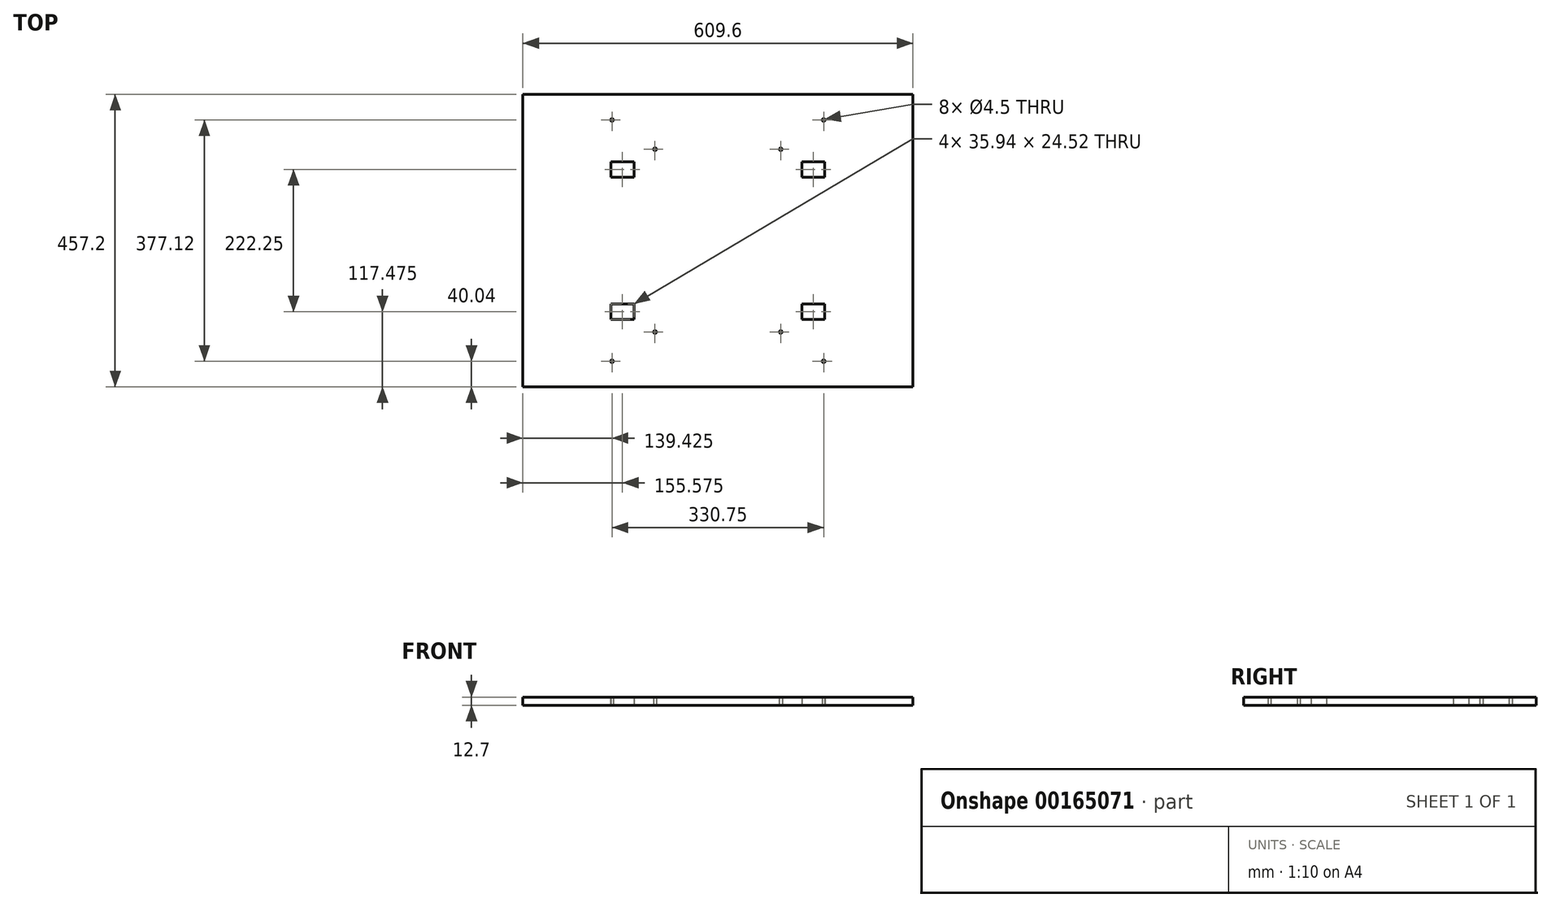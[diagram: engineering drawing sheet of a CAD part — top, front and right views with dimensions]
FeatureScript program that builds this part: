
annotation { "Feature Type Name" : "Feature", "Feature Type Description" : "" }
export const myFeature = defineFeature(function(context is Context, id is Id, definition is map)
    precondition{}
    {
        {
            var Q0;
            Q0=qCreatedBy(makeId("Top.planeOp"),FACE);
            var sketch = newSketch(context, id + "F0", { "sketchPlane" : qUnion([Q0])});
            skLineSegment(sketch, "E0.bottom", {"start": v(-304.8, 228.6) * mm, "end": v(304.8, 228.6) * mm});
            skLineSegment(sketch, "E0.top", {"start": v(-304.8, -228.6) * mm, "end": v(304.8, -228.6) * mm});
            skLineSegment(sketch, "E0.left", {"start": v(-304.8, 228.6) * mm, "end": v(-304.8, -228.6) * mm});
            skLineSegment(sketch, "E0.right", {"start": v(304.8, 228.6) * mm, "end": v(304.8, -228.6) * mm});
            skPoint(sketch, "E0.middle", {"position": v(0, 0) * mm});
            skLineSegment(sketch, "E1.bottom", {"start": v(-149.22, 111.13) * mm, "end": v(149.23, 111.13) * mm, "construction": true});
            skLineSegment(sketch, "E1.top", {"start": v(-149.22, -111.13) * mm, "end": v(149.23, -111.13) * mm, "construction": true});
            skLineSegment(sketch, "E1.left", {"start": v(-149.22, 111.13) * mm, "end": v(-149.22, -111.13) * mm, "construction": true});
            skLineSegment(sketch, "E1.right", {"start": v(149.22, 111.13) * mm, "end": v(149.23, -111.13) * mm, "construction": true});
            skLineSegment(sketch, "E2", {"start": v(98.27, 142.86) * mm, "end": v(149.22, 142.86) * mm, "construction": true});
            skLineSegment(sketch, "E3", {"start": v(149.22, 142.86) * mm, "end": v(165.38, 142.86) * mm, "construction": true});
            skLineSegment(sketch, "E4", {"start": v(165.38, 142.86) * mm, "end": v(165.38, 188.56) * mm, "construction": true});
            skLineSegment(sketch, "E5", {"start": v(149.22, 142.86) * mm, "end": v(149.22, 123.38) * mm, "construction": true});
            skCircle(sketch, "E6", {"center": v(98.27, 142.86) * mm, "radius": 2.25 * mm});
            skCircle(sketch, "E7", {"center": v(165.38, 188.56) * mm, "radius": 2.25 * mm});
            skLineSegment(sketch, "E8.bottom", {"start": v(131.25, 123.38) * mm, "end": v(167.2, 123.38) * mm});
            skLineSegment(sketch, "E8.top", {"start": v(131.25, 98.87) * mm, "end": v(167.2, 98.87) * mm});
            skLineSegment(sketch, "E8.left", {"start": v(131.25, 123.38) * mm, "end": v(131.25, 98.87) * mm});
            skLineSegment(sketch, "E8.right", {"start": v(167.2, 123.38) * mm, "end": v(167.2, 98.87) * mm});
            skPoint(sketch, "E8.middle", {"position": v(149.23, 111.13) * mm});
            skLineSegment(sketch, "E9.bottom", {"start": v(-131.25, 98.87) * mm, "end": v(-167.2, 98.87) * mm});
            skLineSegment(sketch, "E9.top", {"start": v(-131.25, 123.38) * mm, "end": v(-167.2, 123.38) * mm});
            skLineSegment(sketch, "E9.left", {"start": v(-131.25, 98.87) * mm, "end": v(-131.25, 123.38) * mm});
            skLineSegment(sketch, "E9.right", {"start": v(-167.2, 98.87) * mm, "end": v(-167.2, 123.38) * mm});
            skPoint(sketch, "E9.middle", {"position": v(-149.23, 111.13) * mm});
            skLineSegment(sketch, "E10.bottom", {"start": v(-131.25, -123.38) * mm, "end": v(-167.2, -123.38) * mm});
            skLineSegment(sketch, "E10.top", {"start": v(-131.25, -98.87) * mm, "end": v(-167.2, -98.87) * mm});
            skLineSegment(sketch, "E10.left", {"start": v(-131.25, -123.38) * mm, "end": v(-131.25, -98.87) * mm});
            skLineSegment(sketch, "E10.right", {"start": v(-167.2, -123.38) * mm, "end": v(-167.2, -98.87) * mm});
            skPoint(sketch, "E10.middle", {"position": v(-149.23, -111.13) * mm});
            skLineSegment(sketch, "E11.bottom", {"start": v(131.25, -123.38) * mm, "end": v(167.2, -123.38) * mm});
            skLineSegment(sketch, "E11.top", {"start": v(131.25, -98.87) * mm, "end": v(167.2, -98.87) * mm});
            skLineSegment(sketch, "E11.left", {"start": v(131.25, -123.38) * mm, "end": v(131.25, -98.87) * mm});
            skLineSegment(sketch, "E11.right", {"start": v(167.2, -123.38) * mm, "end": v(167.2, -98.87) * mm});
            skPoint(sketch, "E11.middle", {"position": v(149.23, -111.13) * mm});
            skLineSegment(sketch, "E12", {"start": v(-149.22, 123.38) * mm, "end": v(-149.22, 142.86) * mm, "construction": true});
            skLineSegment(sketch, "E13", {"start": v(-149.23, 142.86) * mm, "end": v(-98.27, 142.86) * mm, "construction": true});
            skLineSegment(sketch, "E14", {"start": v(-149.23, 142.86) * mm, "end": v(-165.38, 142.86) * mm, "construction": true});
            skLineSegment(sketch, "E15", {"start": v(-165.38, 142.86) * mm, "end": v(-165.38, 188.56) * mm, "construction": true});
            skLineSegment(sketch, "E16", {"start": v(-149.22, -123.38) * mm, "end": v(-149.22, -142.86) * mm, "construction": true});
            skLineSegment(sketch, "E17", {"start": v(-149.23, -142.86) * mm, "end": v(-165.38, -142.86) * mm, "construction": true});
            skLineSegment(sketch, "E18", {"start": v(-165.38, -142.86) * mm, "end": v(-165.38, -188.56) * mm, "construction": true});
            skLineSegment(sketch, "E19", {"start": v(-149.23, -142.86) * mm, "end": v(-98.27, -142.86) * mm, "construction": true});
            skLineSegment(sketch, "E20", {"start": v(149.22, -123.38) * mm, "end": v(149.22, -142.86) * mm, "construction": true});
            skLineSegment(sketch, "E21", {"start": v(149.22, -142.86) * mm, "end": v(165.38, -142.86) * mm, "construction": true});
            skLineSegment(sketch, "E22", {"start": v(165.38, -142.86) * mm, "end": v(165.38, -188.56) * mm, "construction": true});
            skLineSegment(sketch, "E23", {"start": v(149.22, -142.86) * mm, "end": v(98.27, -142.86) * mm, "construction": true});
            skLineSegment(sketch, "E24.bottom", {"start": v(6.35, 6.35) * mm, "end": v(-6.35, 6.35) * mm, "construction": true});
            skLineSegment(sketch, "E24.top", {"start": v(6.35, -6.35) * mm, "end": v(-6.35, -6.35) * mm, "construction": true});
            skLineSegment(sketch, "E24.left", {"start": v(6.35, 6.35) * mm, "end": v(6.35, -6.35) * mm, "construction": true});
            skLineSegment(sketch, "E24.right", {"start": v(-6.35, 6.35) * mm, "end": v(-6.35, -6.35) * mm, "construction": true});
            skLineSegment(sketch, "E25.bottom", {"start": v(6.35, 6.35) * mm, "end": v(292.1, 6.35) * mm, "construction": true});
            skLineSegment(sketch, "E25.top", {"start": v(6.35, 215.9) * mm, "end": v(292.1, 215.9) * mm, "construction": true});
            skLineSegment(sketch, "E25.left", {"start": v(6.35, 6.35) * mm, "end": v(6.35, 215.9) * mm, "construction": true});
            skLineSegment(sketch, "E25.right", {"start": v(292.1, 6.35) * mm, "end": v(292.1, 215.9) * mm, "construction": true});
            skLineSegment(sketch, "E26", {"start": v(292.1, 215.9) * mm, "end": v(304.8, 215.9) * mm, "construction": true});
            skLineSegment(sketch, "E27", {"start": v(292.1, 215.9) * mm, "end": v(292.1, 228.6) * mm, "construction": true});
            skCircle(sketch, "E28", {"center": v(98.27, -142.86) * mm, "radius": 2.25 * mm});
            skCircle(sketch, "E29", {"center": v(165.38, -188.56) * mm, "radius": 2.25 * mm});
            skCircle(sketch, "E30", {"center": v(-98.27, -142.86) * mm, "radius": 2.25 * mm});
            skCircle(sketch, "E31", {"center": v(-165.38, -188.56) * mm, "radius": 2.25 * mm});
            skCircle(sketch, "E32", {"center": v(-98.27, 142.86) * mm, "radius": 2.25 * mm});
            skCircle(sketch, "E33", {"center": v(-165.38, 188.56) * mm, "radius": 2.25 * mm});
            skSolve(sketch);
        }
        {
            var Q0;
            Q0 = qSketchRegion(id + "F0", true);
            extrude(context, id + "F1", {"entities" : qUnion([Q0]), "depth" : 12.7 * mm});
        }
    });
